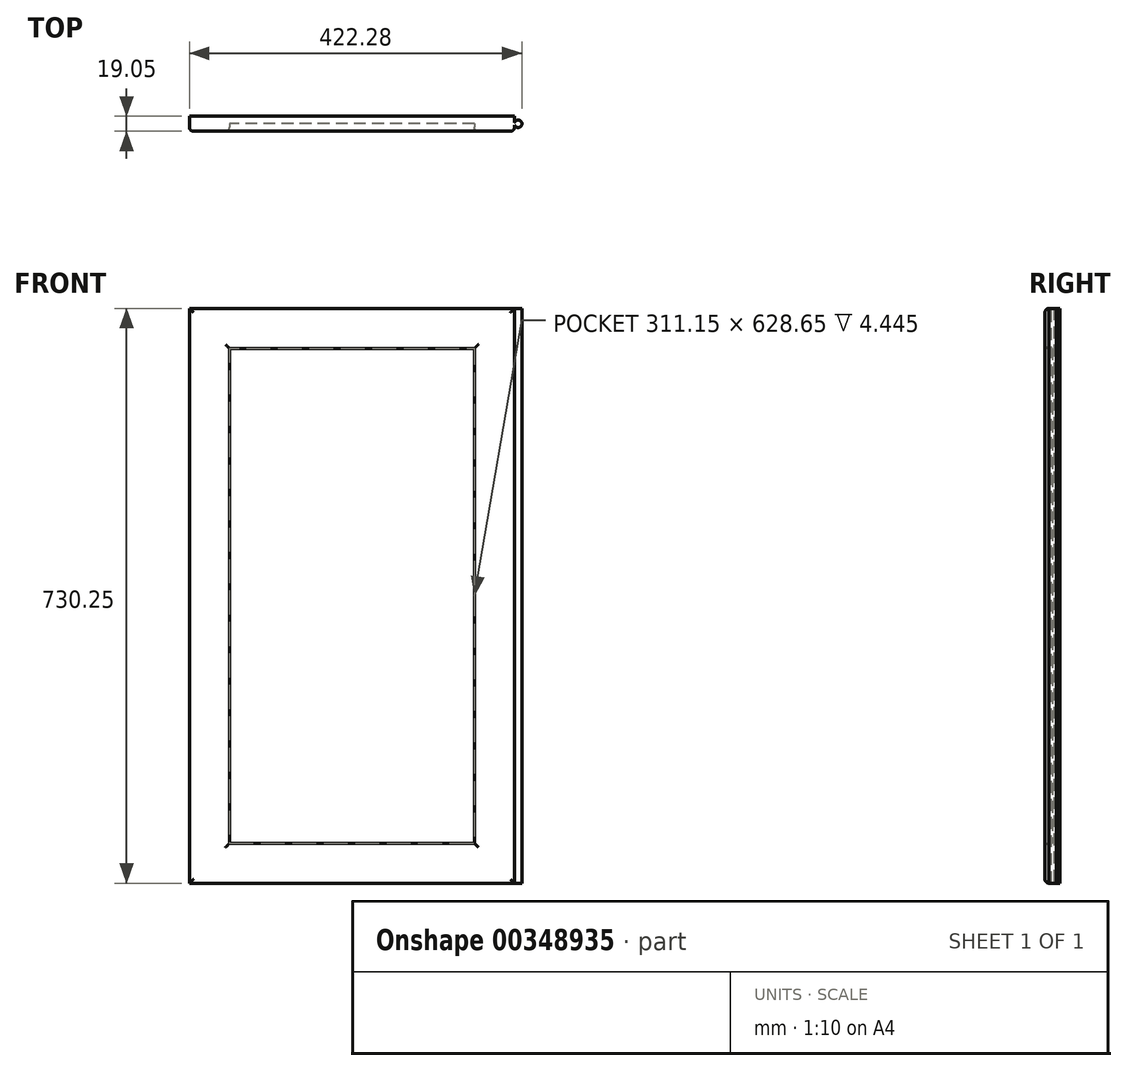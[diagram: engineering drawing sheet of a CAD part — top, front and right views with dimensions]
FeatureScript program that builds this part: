
annotation { "Feature Type Name" : "Feature", "Feature Type Description" : "" }
export const myFeature = defineFeature(function(context is Context, id is Id, definition is map)
    precondition{}
    {
        {
            var Q0;
            Q0=qCreatedBy(makeId("Front.planeOp"),FACE);
            var sketch = newSketch(context, id + "F0", { "sketchPlane" : qUnion([Q0])});
            skLineSegment(sketch, "E0.bottom", {"start": v(-206.37, 0) * mm, "end": v(206.38, 0) * mm});
            skLineSegment(sketch, "E0.top", {"start": v(-206.38, 730.25) * mm, "end": v(206.38, 730.25) * mm});
            skLineSegment(sketch, "E0.left", {"start": v(-206.37, 0) * mm, "end": v(-206.38, 730.25) * mm});
            skLineSegment(sketch, "E0.right", {"start": v(206.38, 0) * mm, "end": v(206.38, 730.25) * mm});
            skPoint(sketch, "E0.middle", {"position": v(0, 365.13) * mm});
            skSolve(sketch);
        }
        {
            var Q0;
            Q0 = qSketchRegion(id + "F0", true);
            extrude(context, id + "F1", {"entities" : qUnion([Q0]), "oppositeDirection" : true, "depth" : 19.05 * mm});
        }
        {
            var Q0;
            Q0=qCreatedBy(makeId("Top.planeOp"),FACE);
            var sketch = newSketch(context, id + "F2", { "sketchPlane" : qUnion([Q0])});
            skArc(sketch, "E1", {"start": v(206.65, 7.94) * mm, "mid": v(215.9, 9.52) * mm, "end": v(206.65, 11.11) * mm});
            skLineSegment(sketch, "E2", {"start": v(206.65, 11.11) * mm, "end": v(204.79, 11.11) * mm});
            skLineSegment(sketch, "E3", {"start": v(204.79, 11.11) * mm, "end": v(204.79, 7.94) * mm});
            skLineSegment(sketch, "E4", {"start": v(204.79, 7.94) * mm, "end": v(206.65, 7.94) * mm});
            skLineSegment(sketch, "E5", {"start": v(204.79, 9.53) * mm, "end": v(211.14, 9.53) * mm, "construction": true});
            skSolve(sketch);
        }
        {
            var Q0;
            Q0 = qSketchRegion(id + "F2", true);
            var Q1;
            Q1=makeQuery(id+"F1.opExtrude","SWEPT_FACE",FACE,{"disambiguationData":[OSD([sQuery(id+"F0.wireOp",EDGE,"E0.top")])]});
            extrude(context, id + "F3", {"entities" : qUnion([Q0]), "operationType" : NewBodyOperationType.ADD, "endBound" : BoundingType.UP_TO_SURFACE, "endBoundEntityFace" : qUnion([Q1]), "depth" : 25.4 * mm});
        }
        {
            var Q0;
            Q0=qCreatedBy(makeId("Front.planeOp"),FACE);
            var sketch = newSketch(context, id + "F4", { "sketchPlane" : qUnion([Q0])});
            skLineSegment(sketch, "E6.bottom", {"start": v(155.57, 679.45) * mm, "end": v(-155.57, 679.45) * mm});
            skLineSegment(sketch, "E6.top", {"start": v(155.57, 50.8) * mm, "end": v(-155.57, 50.8) * mm});
            skLineSegment(sketch, "E6.left", {"start": v(155.57, 679.45) * mm, "end": v(155.57, 50.8) * mm});
            skLineSegment(sketch, "E6.right", {"start": v(-155.58, 679.45) * mm, "end": v(-155.57, 50.8) * mm});
            skPoint(sketch, "E6.middle", {"position": v(0, 365.12) * mm});
            skSolve(sketch);
        }
        {
            var Q0;
            Q0 = qSketchRegion(id + "F4", true);
            extrude(context, id + "F5", {"entities" : qUnion([Q0]), "operationType" : NewBodyOperationType.REMOVE, "oppositeDirection" : true, "depth" : 9.52 * mm});
        }
        {
            var Q0;
            Q0=makeQuery(id+"F1.opExtrude","CAP_FACE",FACE,{"disambiguationData":[OSD([sQuery(id+"F0.wireOp",EDGE,"E0.bottom"),sQuery(id+"F0.wireOp",EDGE,"E0.top"),sQuery(id+"F0.wireOp",EDGE,"E0.left"),sQuery(id+"F0.wireOp",EDGE,"E0.right")])],"isStart":true});
            fillet(context, id + "F6", {"entities" : qUnion([Q0]), "radius" : 5.08 * mm, "tangentPropagation" : true, "allowEdgeOverflow" : false});
        }
    });
